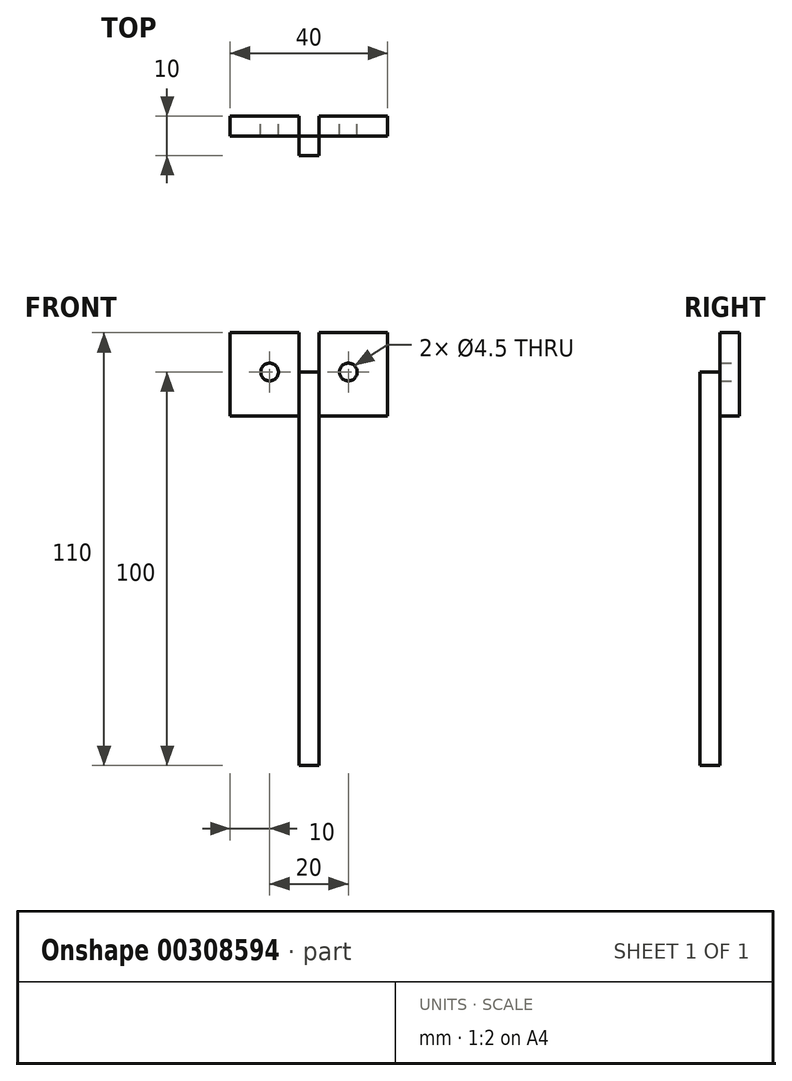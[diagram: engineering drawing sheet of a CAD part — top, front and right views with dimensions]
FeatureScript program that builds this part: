
annotation { "Feature Type Name" : "Feature", "Feature Type Description" : "" }
export const myFeature = defineFeature(function(context is Context, id is Id, definition is map)
    precondition{}
    {
        {
            var Q0;
            Q0=qCreatedBy(makeId("Front.planeOp"),FACE);
            var sketch = newSketch(context, id + "F0", { "sketchPlane" : qUnion([Q0])});
            skLineSegment(sketch, "E0.bottom", {"start": v(-20, 60) * mm, "end": v(20, 60) * mm});
            skLineSegment(sketch, "E0.top", {"start": v(-20, -60) * mm, "end": v(20, -60) * mm});
            skLineSegment(sketch, "E0.left", {"start": v(-20, 60) * mm, "end": v(-20, -60) * mm});
            skLineSegment(sketch, "E0.right", {"start": v(20, 60) * mm, "end": v(20, -60) * mm});
            skPoint(sketch, "E0.middle", {"position": v(0, 0) * mm});
            skPoint(sketch, "E1", {"position": v(-10, 50) * mm});
            skPoint(sketch, "E2", {"position": v(10, 50) * mm});
            skCircle(sketch, "E3", {"center": v(-10, -55) * mm, "radius": 2.25 * mm});
            skCircle(sketch, "E4", {"center": v(10, -55) * mm, "radius": 2.25 * mm});
            skCircle(sketch, "E5", {"center": v(-10, -35) * mm, "radius": 2.25 * mm});
            skCircle(sketch, "E6", {"center": v(10, -35) * mm, "radius": 2.25 * mm});
            skLineSegment(sketch, "E7", {"start": v(-20, -35) * mm, "end": v(20, -35) * mm, "construction": true});
            skLineSegment(sketch, "E8", {"start": v(-20, -55) * mm, "end": v(20, -55) * mm, "construction": true});
            skLineSegment(sketch, "E9", {"start": v(-12.25, -55) * mm, "end": v(-12.25, -35) * mm});
            skLineSegment(sketch, "E10", {"start": v(-7.75, -35) * mm, "end": v(-7.75, -55) * mm});
            skLineSegment(sketch, "E11", {"start": v(7.75, -35) * mm, "end": v(7.75, -55) * mm});
            skLineSegment(sketch, "E12", {"start": v(12.25, -35) * mm, "end": v(12.25, -55) * mm});
            skLineSegment(sketch, "E13.bottom", {"start": v(2.5, 60) * mm, "end": v(-2.5, 60) * mm});
            skLineSegment(sketch, "E13.top", {"start": v(2.5, -60) * mm, "end": v(-2.5, -60) * mm});
            skLineSegment(sketch, "E13.left", {"start": v(2.5, 60) * mm, "end": v(2.5, -60) * mm});
            skLineSegment(sketch, "E13.right", {"start": v(-2.5, 60) * mm, "end": v(-2.5, -60) * mm});
            skLineSegment(sketch, "E14", {"start": v(-20, 38.78) * mm, "end": v(20, 38.78) * mm});
            skSolve(sketch);
        }
        {
            var Q0;
            {var subQ0=sQuery(id+"F0.wireOp",EDGE,"E0.left");Q0=makeQuery(id+"F0.imprint","IMPRINT",FACE,{"disambiguationData":[TD([[makeQuery(id+"F0.imprint","IMPRINT",EDGE,{"derivedFrom":subQ0}),1.0]])]});}
            var Q1;
            Q1=makeQuery(id+"F0.imprint","IMPRINT",FACE,{"disambiguationData":[TD([[makeQuery(id+"F0.imprint","IMPRINT",EDGE,{"derivedFrom":sQuery(id+"F0.wireOp",EDGE,"E13.bottom")}),1.0]])]});
            var Q2;
            {var subQ4=sQuery(id+"F0.wireOp",EDGE,"E0.right");Q2=makeQuery(id+"F0.imprint","IMPRINT",FACE,{"disambiguationData":[TD([[makeQuery(id+"F0.imprint","IMPRINT",EDGE,{"derivedFrom":subQ4}),-1.0]])]});}
            extrude(context, id + "F1", {"entities" : qUnion([Q0, Q1, Q2]), "depth" : 5 * mm});
        }
        {
            var Q0;
            Q0=makeQuery(id+"F1.opExtrude","CAP_FACE",FACE,{"disambiguationData":[OSD([sQuery(id+"F0.wireOp",EDGE,"E0.bottom"),sQuery(id+"F0.wireOp",EDGE,"E0.top"),sQuery(id+"F0.wireOp",EDGE,"E0.left"),sQuery(id+"F0.wireOp",EDGE,"E0.right"),sQuery(id+"F0.wireOp",EDGE,"E3"),sQuery(id+"F0.wireOp",EDGE,"E4"),sQuery(id+"F0.wireOp",EDGE,"E5"),sQuery(id+"F0.wireOp",EDGE,"E6"),sQuery(id+"F0.wireOp",EDGE,"E9"),sQuery(id+"F0.wireOp",EDGE,"E10"),sQuery(id+"F0.wireOp",EDGE,"E11"),sQuery(id+"F0.wireOp",EDGE,"E12"),sQuery(id+"F0.wireOp",EDGE,"E13.bottom"),sQuery(id+"F0.wireOp",EDGE,"E13.top")])],"isStart":false});
            var sketch = newSketch(context, id + "F2", { "sketchPlane" : qUnion([Q0])});
            skLineSegment(sketch, "E15.bottom", {"start": v(2.5, 50) * mm, "end": v(-2.5, 50) * mm});
            skLineSegment(sketch, "E15.top", {"start": v(2.5, -50) * mm, "end": v(-2.5, -50) * mm});
            skLineSegment(sketch, "E15.left", {"start": v(2.5, 50) * mm, "end": v(2.5, -50) * mm});
            skLineSegment(sketch, "E15.right", {"start": v(-2.5, 50) * mm, "end": v(-2.5, -50) * mm});
            skPoint(sketch, "E15.middle", {"position": v(0, 0) * mm});
            skSolve(sketch);
        }
        {
            var Q0;
            Q0=makeQuery(id+"F2.imprint","IMPRINT",FACE,{"disambiguationData":[TD([[makeQuery(id+"F2.imprint","IMPRINT",EDGE,{"derivedFrom":sQuery(id+"F2.wireOp",EDGE,"E15.bottom")}),1.0]])]});
            extrude(context, id + "F3", {"entities" : qUnion([Q0]), "operationType" : NewBodyOperationType.ADD, "depth" : 5 * mm});
        }
        {
            var Q0;
            Q0=sQuery(id+"F0.wireOp",VERTEX,"E2");
            var Q1;
            Q1=sQuery(id+"F0.wireOp",VERTEX,"E1");
            var Q2;
            Q2=makeQuery(id+"F1.opExtrude","SWEPT_BODY",BODY,{"disambiguationData":[OSD([sQuery(id+"F0.wireOp",EDGE,"E0.bottom"),sQuery(id+"F0.wireOp",EDGE,"E0.top"),sQuery(id+"F0.wireOp",EDGE,"E0.left"),sQuery(id+"F0.wireOp",EDGE,"E0.right"),sQuery(id+"F0.wireOp",EDGE,"E3"),sQuery(id+"F0.wireOp",EDGE,"E4"),sQuery(id+"F0.wireOp",EDGE,"E5"),sQuery(id+"F0.wireOp",EDGE,"E6"),sQuery(id+"F0.wireOp",EDGE,"E9"),sQuery(id+"F0.wireOp",EDGE,"E10"),sQuery(id+"F0.wireOp",EDGE,"E11"),sQuery(id+"F0.wireOp",EDGE,"E12"),sQuery(id+"F0.wireOp",EDGE,"E13.bottom"),sQuery(id+"F0.wireOp",EDGE,"E13.top")])]});
            hole(context, id + "F4", {"style" : HoleStyle.SIMPLE, "endStyle" : HoleEndStyle.BLIND, "oppositeDirection" : true, "holeDiameter" : 4.5 * mm, "holeDepth" : 17 * mm, "isTappedThrough" : true, "tappedDepth" : 12 * mm, "tapClearance" : 3, "locations" : qUnion([Q0, Q1]), "scope" : qUnion([Q2])});
        }
    });
